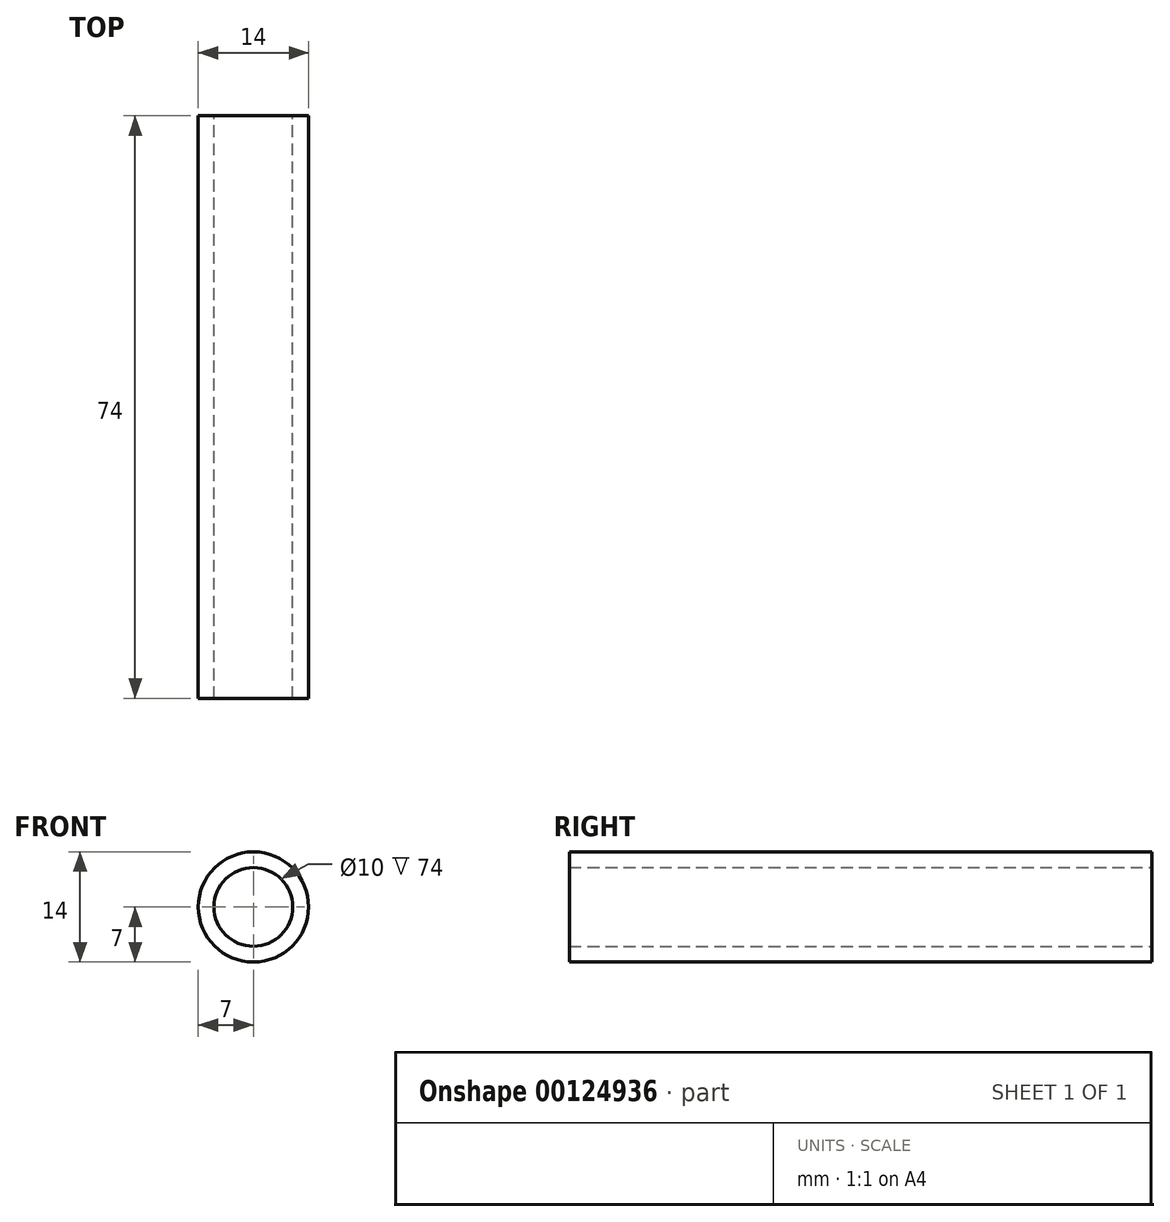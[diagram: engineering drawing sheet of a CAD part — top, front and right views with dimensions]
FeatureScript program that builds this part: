
annotation { "Feature Type Name" : "Feature", "Feature Type Description" : "" }
export const myFeature = defineFeature(function(context is Context, id is Id, definition is map)
    precondition{}
    {
        {
            var Q0;
            Q0=qCreatedBy(makeId("Front.planeOp"),FACE);
            var sketch = newSketch(context, id + "F0", { "sketchPlane" : qUnion([Q0])});
            skCircle(sketch, "E0", {"center": v(0, 0) * mm, "radius": 7 * mm});
            skCircle(sketch, "E1.0", {"center": v(0, 0) * mm, "radius": 5 * mm});
            skSolve(sketch);
        }
        {
            var Q0;
            Q0=makeQuery(id+"F0.imprint","IMPRINT",FACE,{"disambiguationData":[TD([[makeQuery(id+"F0.imprint","IMPRINT",EDGE,{"derivedFrom":sQuery(id+"F0.wireOp",EDGE,"E0")}),1.0]])]});
            extrude(context, id + "F1", {"entities" : qUnion([Q0]), "endBound" : BoundingType.SYMMETRIC, "depth" : 74 * mm});
        }
    });
